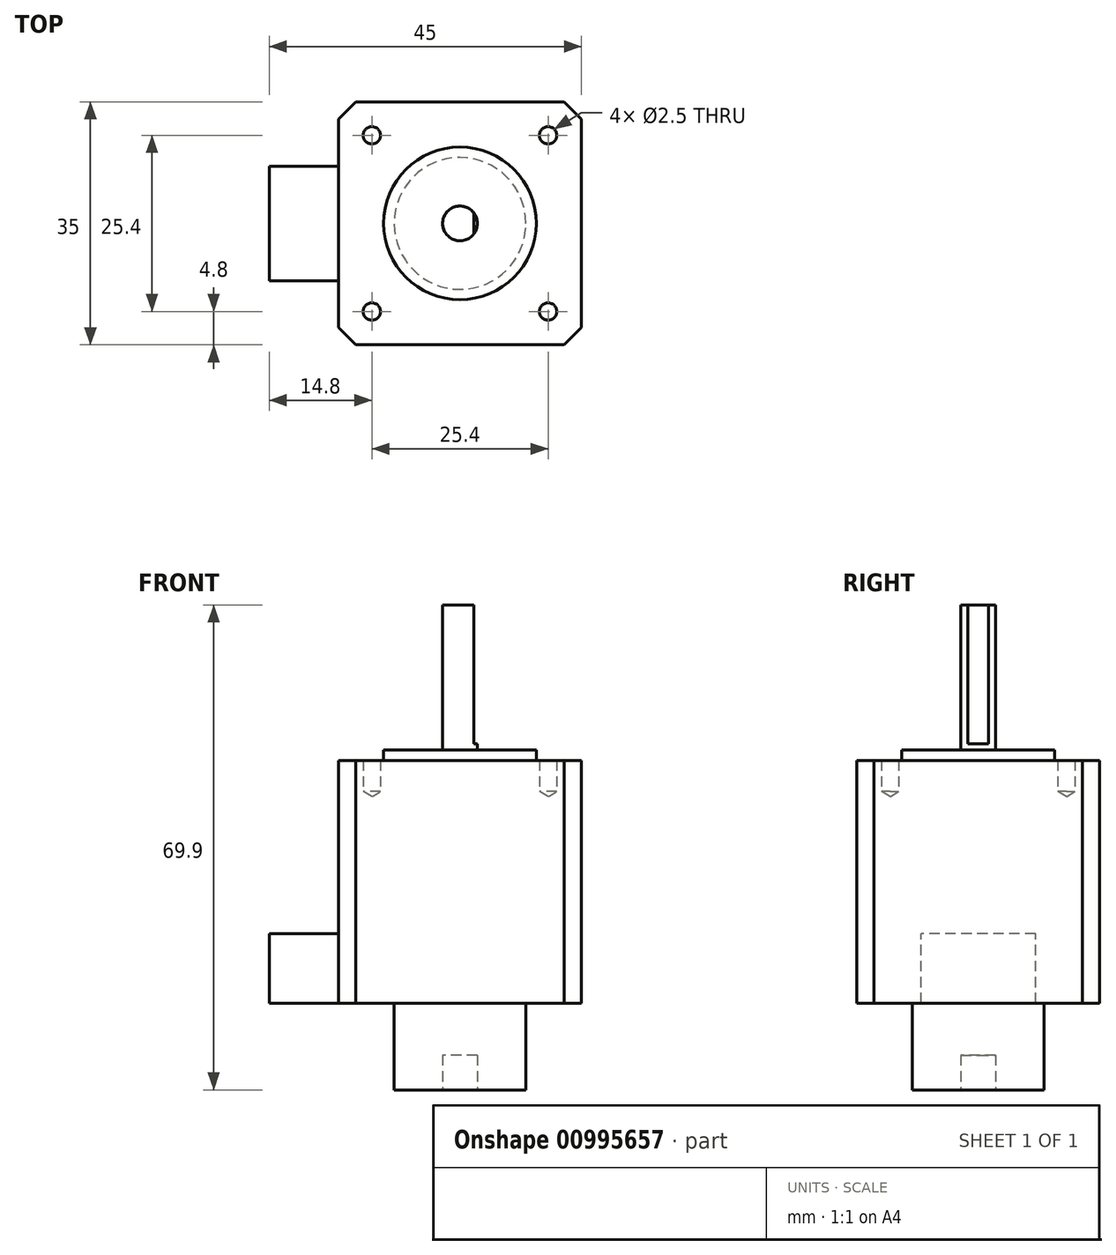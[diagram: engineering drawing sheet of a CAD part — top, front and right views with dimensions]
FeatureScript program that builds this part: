
annotation { "Feature Type Name" : "Feature", "Feature Type Description" : "" }
export const myFeature = defineFeature(function(context is Context, id is Id, definition is map)
    precondition{}
    {
        {
            var Q0;
            Q0=qCreatedBy(makeId("Top.planeOp"),FACE);
            var sketch = newSketch(context, id + "F0", { "sketchPlane" : qUnion([Q0])});
            skLineSegment(sketch, "E0.bottom", {"start": v(-17.5, 17.5) * mm, "end": v(17.5, 17.5) * mm});
            skLineSegment(sketch, "E0.top", {"start": v(-17.5, -17.5) * mm, "end": v(17.5, -17.5) * mm});
            skLineSegment(sketch, "E0.left", {"start": v(-17.5, 17.5) * mm, "end": v(-17.5, -17.5) * mm});
            skLineSegment(sketch, "E0.right", {"start": v(17.5, 17.5) * mm, "end": v(17.5, -17.5) * mm});
            skPoint(sketch, "E0.middle", {"position": v(0, 0) * mm});
            skSolve(sketch);
        }
        {
            var Q0;
            Q0 = qSketchRegion(id + "F0", true);
            extrude(context, id + "F1", {"entities" : qUnion([Q0]), "depth" : 35 * mm, "offsetDistance" : 25 * mm});
        }
        {
            var Q0;
            Q0=makeQuery(id+"F1.opExtrude","SWEPT_EDGE",EDGE,{"disambiguationData":[OSD([sQuery(id+"F0.wireOp",EDGE,"E0.top"),sQuery(id+"F0.wireOp",EDGE,"E0.right")])]});
            var Q1;
            Q1=makeQuery(id+"F1.opExtrude","SWEPT_EDGE",EDGE,{"disambiguationData":[OSD([sQuery(id+"F0.wireOp",EDGE,"E0.top"),sQuery(id+"F0.wireOp",EDGE,"E0.left")])]});
            var Q2;
            Q2=makeQuery(id+"F1.opExtrude","SWEPT_EDGE",EDGE,{"disambiguationData":[OSD([sQuery(id+"F0.wireOp",EDGE,"E0.bottom"),sQuery(id+"F0.wireOp",EDGE,"E0.left")])]});
            var Q3;
            Q3=makeQuery(id+"F1.opExtrude","SWEPT_EDGE",EDGE,{"disambiguationData":[OSD([sQuery(id+"F0.wireOp",EDGE,"E0.bottom"),sQuery(id+"F0.wireOp",EDGE,"E0.right")])]});
            chamfer(context, id + "F2", {"entities" : qUnion([Q0, Q1, Q2, Q3]), "width" : 2.5 * mm, "tangentPropagation" : true});
        }
        {
            var Q0;
            Q0=makeQuery(id+"F1.opExtrude","CAP_FACE",FACE,{"disambiguationData":[OSD([sQuery(id+"F0.wireOp",EDGE,"E0.bottom"),sQuery(id+"F0.wireOp",EDGE,"E0.top"),sQuery(id+"F0.wireOp",EDGE,"E0.left"),sQuery(id+"F0.wireOp",EDGE,"E0.right")])],"isStart":false});
            var sketch = newSketch(context, id + "F3", { "sketchPlane" : qUnion([Q0])});
            skCircle(sketch, "E1", {"center": v(0, 0) * mm, "radius": 11 * mm});
            skSolve(sketch);
        }
        {
            var Q0;
            Q0 = qSketchRegion(id + "F3", true);
            extrude(context, id + "F4", {"entities" : qUnion([Q0]), "operationType" : NewBodyOperationType.ADD, "depth" : 1.5 * mm, "offsetDistance" : 25 * mm});
        }
        {
            var Q0;
            Q0=makeQuery(id+"F4.opExtrude","CAP_FACE",FACE,{"disambiguationData":[OSD([sQuery(id+"F3.wireOp",EDGE,"E1")])],"isStart":false});
            var sketch = newSketch(context, id + "F5", { "sketchPlane" : qUnion([Q0])});
            skCircle(sketch, "E2", {"center": v(0, 0) * mm, "radius": 2.5 * mm});
            skSolve(sketch);
        }
        {
            var Q0;
            Q0 = qSketchRegion(id + "F5", true);
            extrude(context, id + "F6", {"entities" : qUnion([Q0]), "operationType" : NewBodyOperationType.ADD, "depth" : 0.9 * mm, "offsetDistance" : 25 * mm});
        }
        {
            var Q0;
            Q0=makeQuery(id+"F1.opExtrude","SWEPT_FACE",FACE,{"disambiguationData":[OSD([sQuery(id+"F0.wireOp",EDGE,"E0.left")])]});
            var sketch = newSketch(context, id + "F7", { "sketchPlane" : qUnion([Q0])});
            skLineSegment(sketch, "E3.bottom", {"start": v(-8.25, 0) * mm, "end": v(8.25, 0) * mm});
            skLineSegment(sketch, "E3.top", {"start": v(-8.25, 10) * mm, "end": v(8.25, 10) * mm});
            skLineSegment(sketch, "E3.left", {"start": v(-8.25, 0) * mm, "end": v(-8.25, 10) * mm});
            skLineSegment(sketch, "E3.right", {"start": v(8.25, 0) * mm, "end": v(8.25, 10) * mm});
            skPoint(sketch, "E3.middle", {"position": v(0, 5) * mm});
            skPoint(sketch, "E3.middle.positionSnap0", {"position": v(0, 0) * mm});
            skPoint(sketch, "E3.centerSnap0", {"position": v(0, 0) * mm});
            skSolve(sketch);
        }
        {
            var Q0;
            Q0 = qSketchRegion(id + "F7", true);
            extrude(context, id + "F8", {"entities" : qUnion([Q0]), "operationType" : NewBodyOperationType.ADD, "depth" : 10 * mm, "offsetDistance" : 25 * mm});
        }
        {
            var Q0;
            Q0=makeQuery(id+"F6.opExtrude","CAP_FACE",FACE,{"disambiguationData":[OSD([sQuery(id+"F5.wireOp",EDGE,"E2")])],"isStart":false});
            var sketch = newSketch(context, id + "F9", { "sketchPlane" : qUnion([Q0])});
            skArc(sketch, "E4", {"start": v(2, -1.5) * mm, "mid": v(-2.5, 0) * mm, "end": v(2, 1.5) * mm});
            skLineSegment(sketch, "E5", {"start": v(2, 1.5) * mm, "end": v(2, -1.5) * mm});
            skSolve(sketch);
        }
        {
            var Q0;
            Q0 = qSketchRegion(id + "F9", true);
            extrude(context, id + "F10", {"entities" : qUnion([Q0]), "operationType" : NewBodyOperationType.ADD, "depth" : 20 * mm, "offsetDistance" : 25 * mm});
        }
        {
            var Q0;
            Q0=makeQuery(id+"F1.opExtrude","CAP_FACE",FACE,{"disambiguationData":[OSD([sQuery(id+"F0.wireOp",EDGE,"E0.bottom"),sQuery(id+"F0.wireOp",EDGE,"E0.top"),sQuery(id+"F0.wireOp",EDGE,"E0.left"),sQuery(id+"F0.wireOp",EDGE,"E0.right")])],"isStart":false});
            var sketch = newSketch(context, id + "F11", { "sketchPlane" : qUnion([Q0])});
            skPoint(sketch, "E6", {"position": v(12.7, 12.7) * mm});
            skPoint(sketch, "E7", {"position": v(12.7, -12.7) * mm});
            skPoint(sketch, "E8", {"position": v(-12.7, -12.7) * mm});
            skPoint(sketch, "E9", {"position": v(-12.7, 12.7) * mm});
            skSolve(sketch);
        }
        {
            var Q0;
            Q0=sQuery(id+"F11.wireOp",VERTEX,"E9");
            var Q1;
            Q1=sQuery(id+"F11.wireOp",VERTEX,"E6");
            var Q2;
            Q2=sQuery(id+"F11.wireOp",VERTEX,"E7");
            var Q3;
            Q3=sQuery(id+"F11.wireOp",VERTEX,"E8");
            var Q4;
            Q4=makeQuery(id+"F1.opExtrude","SWEPT_BODY",BODY,{"disambiguationData":[OSD([sQuery(id+"F0.wireOp",EDGE,"E0.bottom"),sQuery(id+"F0.wireOp",EDGE,"E0.top"),sQuery(id+"F0.wireOp",EDGE,"E0.left"),sQuery(id+"F0.wireOp",EDGE,"E0.right")])]});
            hole(context, id + "F12", {"style" : HoleStyle.SIMPLE, "endStyle" : HoleEndStyle.BLIND, "standardTappedOrClearance" : lookupTablePath({ "standard" : "ISO", "engagement" : "75%", "pitch" : "0.5 mm", "size" : "M3", "type" : "Tapped" }), "standardBlindInLast" : lookupTablePath({ "standard" : "ISO", "fit" : "Normal", "engagement" : "75%", "pitch" : "0.5 mm", "size" : "M3", "type" : "Clearance & tapped" }), "holeDiameter" : 2.5 * mm, "majorDiameter" : 3 * mm, "showTappedDepth" : true, "holeDepth" : 4.5 * mm, "isTappedThrough" : true, "tappedDepth" : 3 * mm, "tapClearance" : 3, "locations" : qUnion([Q0, Q1, Q2, Q3]), "scope" : qUnion([Q4])});
        }
        {
            var Q0;
            Q0=qCreatedBy(makeId("Front.planeOp"),FACE);
            var sketch = newSketch(context, id + "F13", { "sketchPlane" : qUnion([Q0])});
            skLineSegment(sketch, "E10", {"start": v(0, -8) * mm, "end": v(0, 8) * mm, "construction": true});
            skLineSegment(sketch, "E11", {"start": v(8.9, 8) * mm, "end": v(8.9, 6.9) * mm});
            skLineSegment(sketch, "E12", {"start": v(8.9, 6.9) * mm, "end": v(6, 6.9) * mm});
            skLineSegment(sketch, "E13", {"start": v(6, 6.9) * mm, "end": v(6, -0.5) * mm});
            skLineSegment(sketch, "E14", {"start": v(6, -0.5) * mm, "end": v(8.9, -0.5) * mm});
            skLineSegment(sketch, "E15", {"start": v(8.9, -0.5) * mm, "end": v(8.9, -8) * mm});
            skLineSegment(sketch, "E16", {"start": v(8.9, -8) * mm, "end": v(2.5, -8) * mm});
            skLineSegment(sketch, "E17", {"start": v(2.5, -8) * mm, "end": v(2.5, 8) * mm});
            skLineSegment(sketch, "E18", {"start": v(2.5, 8) * mm, "end": v(8.9, 8) * mm});
            skSolve(sketch);
        }
        {
            var Q0;
            Q0 = qSketchRegion(id + "F13", true);
            var Q1;
            Q1=sQuery(id+"F13.wireOp",EDGE,"E10");
            revolve(context, id + "F14", {"surfaceOperationType" : NewSurfaceOperationType.NEW, "entities" : qUnion([Q0]), "axis" : qUnion([Q1]), "revolveType" : RevolveType.FULL});
        }
        {
            var Q0;
            Q0=qCreatedBy(makeId("Front.planeOp"),FACE);
            var sketch = newSketch(context, id + "F15", { "sketchPlane" : qUnion([Q0])});
            skLineSegment(sketch, "E19", {"start": v(0, -4.25) * mm, "end": v(0, 4.25) * mm, "construction": true});
            skLineSegment(sketch, "E20", {"start": v(2.5, -4.25) * mm, "end": v(2.5, 4.25) * mm});
            skLineSegment(sketch, "E21", {"start": v(2.5, 4.25) * mm, "end": v(9, 4.25) * mm});
            skLineSegment(sketch, "E22", {"start": v(9, 4.25) * mm, "end": v(9, 3.25) * mm});
            skLineSegment(sketch, "E23", {"start": v(9, 3.25) * mm, "end": v(6, 3.25) * mm});
            skLineSegment(sketch, "E24", {"start": v(6, 3.25) * mm, "end": v(6, -3.25) * mm});
            skLineSegment(sketch, "E25", {"start": v(6, -3.25) * mm, "end": v(9, -3.25) * mm});
            skLineSegment(sketch, "E26", {"start": v(9, -3.25) * mm, "end": v(9, -4.25) * mm});
            skLineSegment(sketch, "E27", {"start": v(9, -4.25) * mm, "end": v(2.5, -4.25) * mm});
            skSolve(sketch);
        }
        {
            var Q0;
            Q0 = qSketchRegion(id + "F15", true);
            var Q1;
            Q1=sQuery(id+"F15.wireOp",EDGE,"E19");
            revolve(context, id + "F16", {"surfaceOperationType" : NewSurfaceOperationType.NEW, "entities" : qUnion([Q0]), "axis" : qUnion([Q1]), "revolveType" : RevolveType.FULL});
        }
        {
            var Q0;
            Q0=qCreatedBy(makeId("Front.planeOp"),FACE);
            var sketch = newSketch(context, id + "F17", { "sketchPlane" : qUnion([Q0])});
            skLineSegment(sketch, "E28", {"start": v(-3, 0) * mm, "end": v(-3, -9.5) * mm});
            skLineSegment(sketch, "E29", {"start": v(-3, -9.5) * mm, "end": v(-6, -9.5) * mm});
            skLineSegment(sketch, "E30", {"start": v(-6, -9.5) * mm, "end": v(-6, -6.9) * mm});
            skLineSegment(sketch, "E31", {"start": v(-6, -6.9) * mm, "end": v(-5.7, -6.9) * mm});
            skLineSegment(sketch, "E32", {"start": v(-5.7, -6.9) * mm, "end": v(-5.7, -5.9) * mm});
            skLineSegment(sketch, "E33", {"start": v(-5.7, -5.9) * mm, "end": v(-6, -5.9) * mm});
            skLineSegment(sketch, "E34", {"start": v(-6, -5.9) * mm, "end": v(-6, 0) * mm});
            skLineSegment(sketch, "E35", {"start": v(-6, 0) * mm, "end": v(-3, 0) * mm});
            skLineSegment(sketch, "E36", {"start": v(0, -9.5) * mm, "end": v(0, 0) * mm, "construction": true});
            skLineSegment(sketch, "E37", {"start": v(-6, 0) * mm, "end": v(0, 0) * mm, "construction": true});
            skSolve(sketch);
        }
        {
            var Q0;
            Q0=makeQuery(id+"F17.imprint","IMPRINT",FACE,{"disambiguationData":[TD([[makeQuery(id+"F17.imprint","IMPRINT",EDGE,{"derivedFrom":sQuery(id+"F17.wireOp",EDGE,"E28")}),-1.0]])]});
            var Q1;
            Q1=sQuery(id+"F17.wireOp",EDGE,"E36");
            revolve(context, id + "F18", {"surfaceOperationType" : NewSurfaceOperationType.NEW, "entities" : qUnion([Q0]), "axis" : qUnion([Q1]), "revolveType" : RevolveType.FULL});
        }
        {
            var Q0;
            Q0=makeQuery(id+"F18.opRevolve","SWEPT_BODY",BODY,{"disambiguationData":[OSD([sQuery(id+"F17.wireOp",EDGE,"E28"),sQuery(id+"F17.wireOp",EDGE,"E29"),sQuery(id+"F17.wireOp",EDGE,"E30"),sQuery(id+"F17.wireOp",EDGE,"E31"),sQuery(id+"F17.wireOp",EDGE,"E32"),sQuery(id+"F17.wireOp",EDGE,"E33"),sQuery(id+"F17.wireOp",EDGE,"E34"),sQuery(id+"F17.wireOp",EDGE,"E35")])]});
            var Q1;
            Q1=qCreatedBy(makeId("Top.planeOp"),FACE);
            mirror(context, id + "F19", {"operationType" : NewBodyOperationType.ADD, "entities" : qUnion([Q0]), "mirrorPlane" : qUnion([Q1])});
        }
        {
            var Q0;
            Q0=qCreatedBy(makeId("Top.planeOp"),FACE);
            var sketch = newSketch(context, id + "F20", { "sketchPlane" : qUnion([Q0])});
            skCircle(sketch, "E38", {"center": v(0, 0) * mm, "radius": 2.5 * mm});
            skCircle(sketch, "E39", {"center": v(0, 0) * mm, "radius": 9.5 * mm});
            skSolve(sketch);
        }
        {
            var Q0;
            Q0 = qSketchRegion(id + "F20", true);
            extrude(context, id + "F21", {"entities" : qUnion([Q0]), "depth" : 25 * mm, "offsetDistance" : 25 * mm, "symmetric" : true});
        }
        {
            var Q0;
            Q0=makeQuery(id+"F20.imprint","IMPRINT",FACE,{"disambiguationData":[TD([[makeQuery(id+"F20.imprint","IMPRINT",EDGE,{"derivedFrom":sQuery(id+"F20.wireOp",EDGE,"E38")}),1.0]])]});
            extrude(context, id + "F22", {"entities" : qUnion([Q0]), "operationType" : NewBodyOperationType.ADD, "depth" : 15 * mm, "offsetDistance" : 25 * mm, "symmetric" : true});
        }
    });
